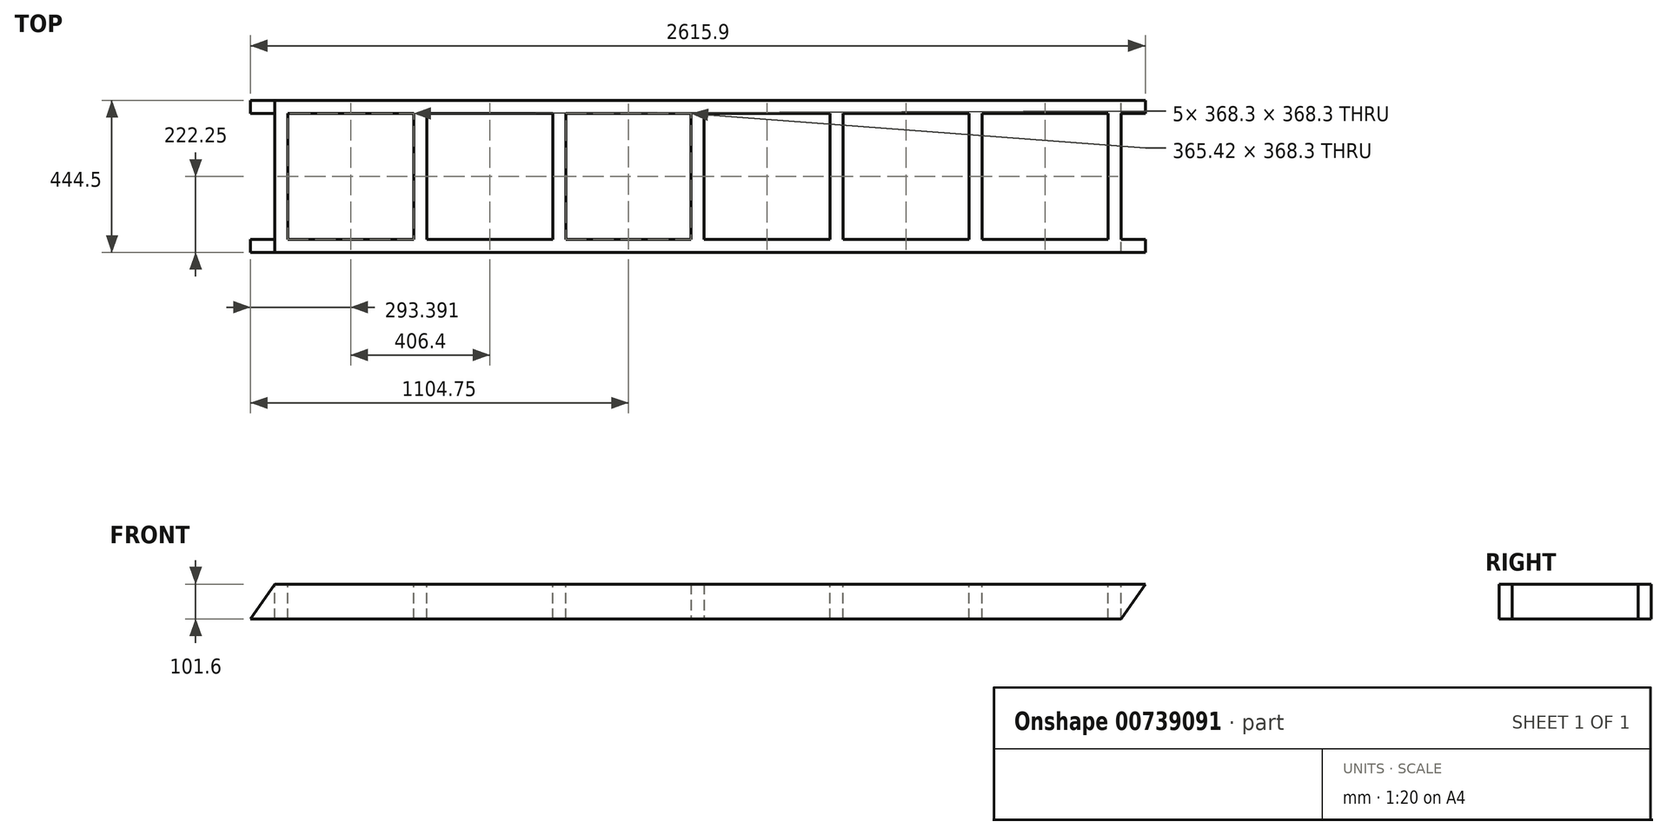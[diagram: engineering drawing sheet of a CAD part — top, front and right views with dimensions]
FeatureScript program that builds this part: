
annotation { "Feature Type Name" : "Feature", "Feature Type Description" : "" }
export const myFeature = defineFeature(function(context is Context, id is Id, definition is map)
    precondition{}
    {
        {
            var Q0;
            Q0=qCreatedBy(makeId("Front.planeOp"),FACE);
            var sketch = newSketch(context, id + "F0", { "sketchPlane" : qUnion([Q0])});
            skLineSegment(sketch, "E0", {"start": v(0, 0) * mm, "end": v(2544.76, 0) * mm});
            skLineSegment(sketch, "E1", {"start": v(0, 0) * mm, "end": v(71.14, 101.6) * mm});
            skLineSegment(sketch, "E2", {"start": v(71.14, 101.6) * mm, "end": v(2615.9, 101.6) * mm});
            skLineSegment(sketch, "E3", {"start": v(2544.76, 0) * mm, "end": v(2615.9, 101.6) * mm});
            skLineSegment(sketch, "E4", {"start": v(0, 0) * mm, "end": v(0, 595.6) * mm, "construction": true});
            skLineSegment(sketch, "E5", {"start": v(2615.9, 101.6) * mm, "end": v(2615.9, 589.03) * mm, "construction": true});
            skLineSegment(sketch, "E6", {"start": v(0, 501.48) * mm, "end": v(2615.9, 501.48) * mm, "construction": true});
            skLineSegment(sketch, "E7", {"start": v(1307.95, 501.48) * mm, "end": v(1307.95, -623.54) * mm, "construction": true});
            skSolve(sketch);
        }
        {
            var Q0;
            Q0=makeQuery(id+"F0.imprint","IMPRINT",FACE,{"disambiguationData":[TD([[makeQuery(id+"F0.imprint","IMPRINT",EDGE,{"derivedFrom":sQuery(id+"F0.wireOp",EDGE,"A8Y6bzSC-6r7V-lSMC-JoRm-8fB1DpuFeBPZ")}),1.0]])]});
            var Q1;
            Q1=makeQuery(id+"F0.imprint","IMPRINT",FACE,{"disambiguationData":[TD([[makeQuery(id+"F0.imprint","IMPRINT",EDGE,{"derivedFrom":sQuery(id+"F0.wireOp",EDGE,"E0")}),1.0]])]});
            extrude(context, id + "F1", {"entities" : qUnion([Q0, Q1]), "depth" : 38.1 * mm, "offsetDistance" : 25.4 * mm});
        }
        {
            var Q0;
            Q0=makeQuery(id+"F1.opExtrude","CAP_FACE",FACE,{"disambiguationData":[OSD([sQuery(id+"F0.wireOp",EDGE,"E0"),sQuery(id+"F0.wireOp",EDGE,"E1"),sQuery(id+"F0.wireOp",EDGE,"E2"),sQuery(id+"F0.wireOp",EDGE,"E3")])],"isStart":false});
            var sketch = newSketch(context, id + "F2", { "sketchPlane" : qUnion([Q0])});
            skLineSegment(sketch, "E8", {"start": v(0, 0) * mm, "end": v(0, 599.17) * mm, "construction": true});
            skLineSegment(sketch, "E9", {"start": v(2615.9, 101.6) * mm, "end": v(2615.9, 656.04) * mm, "construction": true});
            skLineSegment(sketch, "E10", {"start": v(0, 487.8) * mm, "end": v(2615.9, 487.8) * mm, "construction": true});
            skLineSegment(sketch, "E11", {"start": v(1307.95, 487.8) * mm, "end": v(1307.95, -358.16) * mm, "construction": true});
            skLineSegment(sketch, "E12.bottom", {"start": v(2544.76, 0) * mm, "end": v(2506.66, 0) * mm});
            skLineSegment(sketch, "E12.top", {"start": v(2544.76, 101.6) * mm, "end": v(2506.66, 101.6) * mm});
            skLineSegment(sketch, "E12.left", {"start": v(2544.76, 0) * mm, "end": v(2544.76, 101.6) * mm});
            skLineSegment(sketch, "E12.right", {"start": v(2506.66, 0) * mm, "end": v(2506.66, 101.6) * mm});
            skLineSegment(sketch, "E13.bottom", {"start": v(2138.36, 0) * mm, "end": v(2100.26, 0) * mm});
            skLineSegment(sketch, "E13.top", {"start": v(2138.36, 101.6) * mm, "end": v(2100.26, 101.6) * mm});
            skLineSegment(sketch, "E13.left", {"start": v(2138.36, 0) * mm, "end": v(2138.36, 101.6) * mm});
            skLineSegment(sketch, "E13.right", {"start": v(2100.26, 0) * mm, "end": v(2100.26, 101.6) * mm});
            skLineSegment(sketch, "E14.bottom", {"start": v(1731.96, 0) * mm, "end": v(1693.86, 0) * mm});
            skLineSegment(sketch, "E14.top", {"start": v(1731.96, 101.6) * mm, "end": v(1693.86, 101.6) * mm});
            skLineSegment(sketch, "E14.left", {"start": v(1731.96, 0) * mm, "end": v(1731.96, 101.6) * mm});
            skLineSegment(sketch, "E14.right", {"start": v(1693.86, 0) * mm, "end": v(1693.86, 101.6) * mm});
            skLineSegment(sketch, "E15.bottom", {"start": v(1287.46, 101.6) * mm, "end": v(1325.56, 101.6) * mm});
            skLineSegment(sketch, "E15.top", {"start": v(1287.46, 0) * mm, "end": v(1325.56, 0) * mm});
            skLineSegment(sketch, "E15.left", {"start": v(1287.46, 101.6) * mm, "end": v(1287.46, 0) * mm});
            skLineSegment(sketch, "E15.right", {"start": v(1325.56, 101.6) * mm, "end": v(1325.56, 0) * mm});
            skLineSegment(sketch, "E16.MirrorCS", {"start": v(883.94, 101.6) * mm, "end": v(922.04, 101.6) * mm});
            skLineSegment(sketch, "E17.MirrorCS", {"start": v(883.94, 0) * mm, "end": v(922.04, 0) * mm});
            skLineSegment(sketch, "E18.MirrorCS", {"start": v(477.54, 101.6) * mm, "end": v(515.64, 101.6) * mm});
            skLineSegment(sketch, "E19.MirrorCS", {"start": v(71.14, 0) * mm, "end": v(109.24, 0) * mm});
            skLineSegment(sketch, "E20.MirrorCS", {"start": v(71.14, 101.6) * mm, "end": v(109.24, 101.6) * mm});
            skLineSegment(sketch, "E21.MirrorCS", {"start": v(477.54, 0) * mm, "end": v(515.64, 0) * mm});
            skLineSegment(sketch, "E22.MirrorCS", {"start": v(477.54, 0) * mm, "end": v(477.54, 101.6) * mm});
            skLineSegment(sketch, "E23.MirrorCS", {"start": v(109.24, 0) * mm, "end": v(109.24, 101.6) * mm});
            skLineSegment(sketch, "E24.MirrorCS", {"start": v(922.04, 0) * mm, "end": v(922.04, 101.6) * mm});
            skLineSegment(sketch, "E25.MirrorCS", {"start": v(883.94, 0) * mm, "end": v(883.94, 101.6) * mm});
            skLineSegment(sketch, "E26.MirrorCS", {"start": v(71.14, 0) * mm, "end": v(71.14, 101.6) * mm});
            skLineSegment(sketch, "E27.MirrorCS", {"start": v(515.64, 0) * mm, "end": v(515.64, 101.6) * mm});
            skSolve(sketch);
        }
        {
            var Q0;
            Q0=makeQuery(id+"F2.imprint","IMPRINT",FACE,{"disambiguationData":[TD([[makeQuery(id+"F2.imprint","IMPRINT",EDGE,{"derivedFrom":sQuery(id+"F2.wireOp",EDGE,"E19.MirrorCS")}),1.0]])]});
            var Q1;
            Q1=makeQuery(id+"F2.imprint","IMPRINT",FACE,{"disambiguationData":[TD([[makeQuery(id+"F2.imprint","IMPRINT",EDGE,{"derivedFrom":sQuery(id+"F2.wireOp",EDGE,"E18.MirrorCS")}),-1.0]])]});
            var Q2;
            Q2=makeQuery(id+"F2.imprint","IMPRINT",FACE,{"disambiguationData":[TD([[makeQuery(id+"F2.imprint","IMPRINT",EDGE,{"derivedFrom":sQuery(id+"F2.wireOp",EDGE,"E16.MirrorCS")}),-1.0]])]});
            var Q3;
            Q3=makeQuery(id+"F2.imprint","IMPRINT",FACE,{"disambiguationData":[TD([[makeQuery(id+"F2.imprint","IMPRINT",EDGE,{"derivedFrom":sQuery(id+"F2.wireOp",EDGE,"E15.bottom")}),-1.0]])]});
            var Q4;
            Q4=makeQuery(id+"F2.imprint","IMPRINT",FACE,{"disambiguationData":[TD([[makeQuery(id+"F2.imprint","IMPRINT",EDGE,{"derivedFrom":sQuery(id+"F2.wireOp",EDGE,"E14.bottom")}),1.0]])]});
            var Q5;
            Q5=makeQuery(id+"F2.imprint","IMPRINT",FACE,{"disambiguationData":[TD([[makeQuery(id+"F2.imprint","IMPRINT",EDGE,{"derivedFrom":sQuery(id+"F2.wireOp",EDGE,"E13.bottom")}),1.0]])]});
            var Q6;
            Q6=makeQuery(id+"F2.imprint","IMPRINT",FACE,{"disambiguationData":[TD([[makeQuery(id+"F2.imprint","IMPRINT",EDGE,{"derivedFrom":sQuery(id+"F2.wireOp",EDGE,"E12.bottom")}),1.0]])]});
            extrude(context, id + "F3", {"entities" : qUnion([Q0, Q1, Q2, Q3, Q4, Q5, Q6]), "operationType" : NewBodyOperationType.ADD, "depth" : 368.3 * mm, "offsetDistance" : 25.4 * mm});
        }
        {
            var Q0;
            Q0=makeQuery(id+"F3.opExtrude","CAP_FACE",FACE,{"disambiguationData":[OSD([sQuery(id+"F2.wireOp",EDGE,"E19.MirrorCS"),sQuery(id+"F2.wireOp",EDGE,"E20.MirrorCS"),sQuery(id+"F2.wireOp",EDGE,"E23.MirrorCS"),sQuery(id+"F2.wireOp",EDGE,"E26.MirrorCS")])],"isStart":false});
            var sketch = newSketch(context, id + "F4", { "sketchPlane" : qUnion([Q0])});
            skLineSegment(sketch, "E28.0", {"start": v(0, 0) * mm, "end": v(71.14, 101.6) * mm});
            skLineSegment(sketch, "E29.0", {"start": v(2544.76, 0) * mm, "end": v(2615.9, 101.6) * mm});
            skLineSegment(sketch, "E30", {"start": v(71.14, 101.6) * mm, "end": v(2615.9, 101.6) * mm});
            skLineSegment(sketch, "E31", {"start": v(0, 0) * mm, "end": v(2544.76, 0) * mm});
            skSolve(sketch);
        }
        {
            var Q0;
            {var subQ0=sQuery(id+"F4.wireOp",EDGE,"E29.0");Q0=makeQuery(id+"F4.imprint","IMPRINT",FACE,{"disambiguationData":[TD([[makeQuery(id+"F4.imprint","IMPRINT",EDGE,{"derivedFrom":subQ0}),1.0]])]});}
            var Q1;
            {var subQ2=makeQuery(id+"F3.opExtrude","CAP_EDGE",EDGE,{"disambiguationData":[OSD([sQuery(id+"F2.wireOp",EDGE,"E23.MirrorCS")])],"isStart":false});Q1=makeQuery(id+"F4.imprint","IMPRINT",FACE,{"disambiguationData":[TD([[makeQuery(id+"F4.imprint","IMPRINT",EDGE,{"derivedFrom":subQ2}),1.0]])]});}
            var Q2;
            {var subQ0=sQuery(id+"F4.wireOp",EDGE,"E28.0");Q2=makeQuery(id+"F4.imprint","IMPRINT",FACE,{"disambiguationData":[TD([[makeQuery(id+"F4.imprint","IMPRINT",EDGE,{"derivedFrom":subQ0}),-1.0]])]});}
            extrude(context, id + "F5", {"entities" : qUnion([Q0, Q1, Q2]), "operationType" : NewBodyOperationType.ADD, "depth" : 38.1 * mm, "offsetDistance" : 25.4 * mm});
        }
    });
